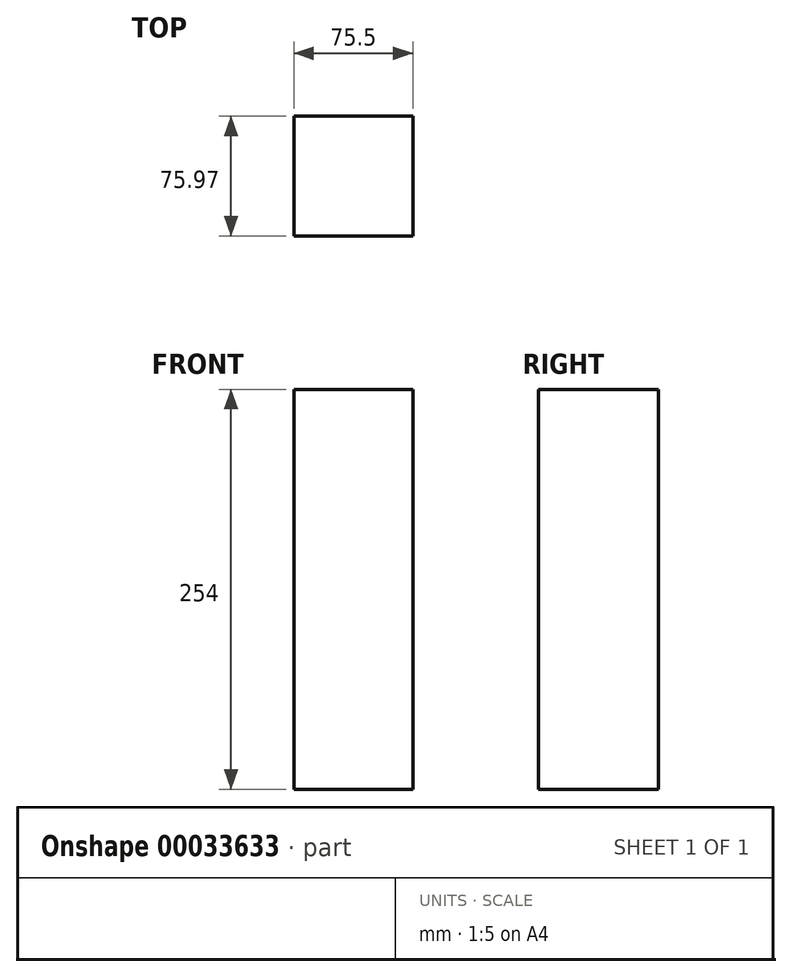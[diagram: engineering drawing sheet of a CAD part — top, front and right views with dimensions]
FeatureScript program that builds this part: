
annotation { "Feature Type Name" : "Feature", "Feature Type Description" : "" }
export const myFeature = defineFeature(function(context is Context, id is Id, definition is map)
    precondition{}
    {
        {
            var Q0;
            Q0=qCreatedBy(makeId("Top.planeOp"),FACE);
            var sketch = newSketch(context, id + "F0", { "sketchPlane" : qUnion([Q0])});
            skLineSegment(sketch, "E0.bottom", {"start": v(0, 0) * mm, "end": v(75.5, 0) * mm});
            skLineSegment(sketch, "E0.top", {"start": v(0, 75.97) * mm, "end": v(75.5, 75.97) * mm});
            skLineSegment(sketch, "E0.left", {"start": v(0, 0) * mm, "end": v(0, 75.97) * mm});
            skLineSegment(sketch, "E0.right", {"start": v(75.5, 0) * mm, "end": v(75.5, 75.97) * mm});
            skSolve(sketch);
        }
        {
            var Q0;
            Q0=makeQuery(id+"F0.imprint","IMPRINT",FACE,{"disambiguationData":[TD([[makeQuery(id+"F0.imprint","IMPRINT",EDGE,{"derivedFrom":sQuery(id+"F0.wireOp",EDGE,"E0.bottom")}),1.0]])]});
            extrude(context, id + "F1", {"entities" : qUnion([Q0]), "oppositeDirection" : true, "depth" : 254 * mm});
        }
    });
